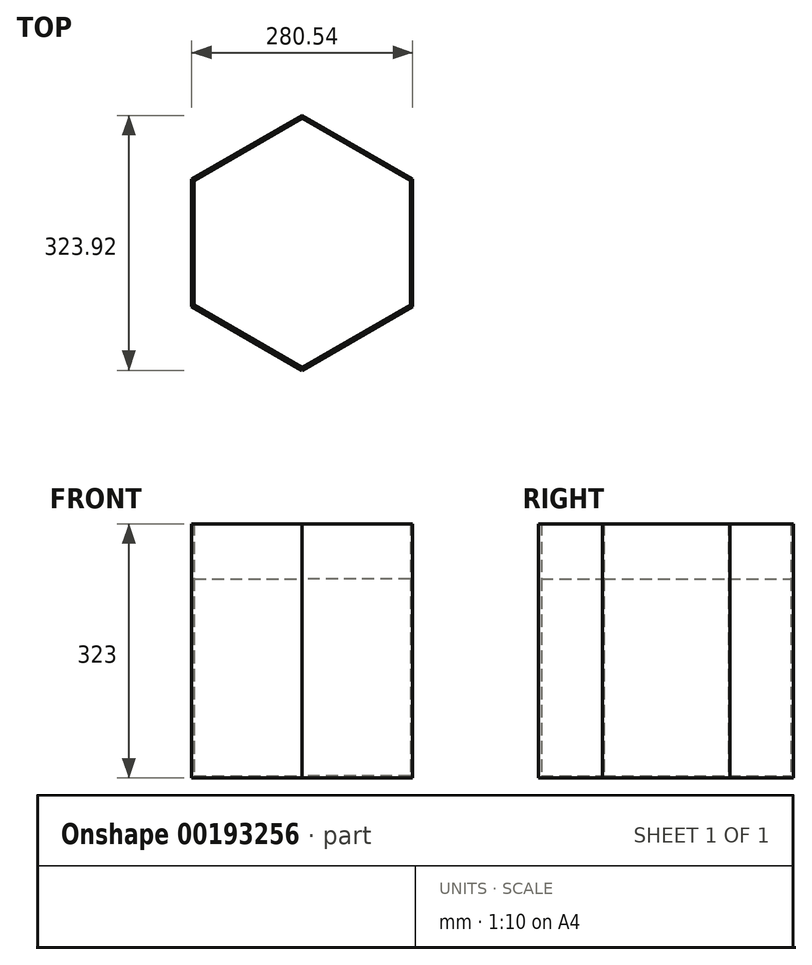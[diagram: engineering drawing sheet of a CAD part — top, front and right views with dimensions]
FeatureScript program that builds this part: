
annotation { "Feature Type Name" : "Feature", "Feature Type Description" : "" }
export const myFeature = defineFeature(function(context is Context, id is Id, definition is map)
    precondition{}
    {
        {
            var Q0;
            Q0=qCreatedBy(makeId("Top.planeOp"),FACE);
            var sketch = newSketch(context, id + "F0", { "sketchPlane" : qUnion([Q0])});
            skCircle(sketch, "E0.cCircle", {"center": v(0, 0) * mm, "radius": 158.5 * mm, "construction": true});
            skLineSegment(sketch, "E0.0", {"start": v(0, 158.5) * mm, "end": v(137.27, 79.25) * mm});
            skLineSegment(sketch, "E0.1", {"start": v(137.27, 79.25) * mm, "end": v(137.27, -79.25) * mm});
            skLineSegment(sketch, "E0.2", {"start": v(137.27, -79.25) * mm, "end": v(0, -158.5) * mm});
            skLineSegment(sketch, "E0.3", {"start": v(0, -158.5) * mm, "end": v(-137.27, -79.25) * mm});
            skLineSegment(sketch, "E0.4", {"start": v(-137.27, -79.25) * mm, "end": v(-137.27, 79.25) * mm});
            skLineSegment(sketch, "E0.5", {"start": v(-137.27, 79.25) * mm, "end": v(0, 158.5) * mm});
            skCircle(sketch, "E1.cCircle", {"center": v(0, 0) * mm, "radius": 161.96 * mm, "construction": true});
            skLineSegment(sketch, "E1.0", {"start": v(0, 161.96) * mm, "end": v(140.27, 80.98) * mm});
            skLineSegment(sketch, "E1.1", {"start": v(140.27, 80.98) * mm, "end": v(140.27, -80.98) * mm});
            skLineSegment(sketch, "E1.2", {"start": v(140.27, -80.98) * mm, "end": v(0, -161.96) * mm});
            skLineSegment(sketch, "E1.3", {"start": v(0, -161.96) * mm, "end": v(-140.27, -80.98) * mm});
            skLineSegment(sketch, "E1.4", {"start": v(-140.27, -80.98) * mm, "end": v(-140.27, 80.98) * mm});
            skLineSegment(sketch, "E1.5", {"start": v(-140.27, 80.98) * mm, "end": v(0, 161.96) * mm});
            skSolve(sketch);
        }
        {
            var Q0;
            Q0 = qSketchRegion(id + "F0", true);
            var Q1;
            Q1=makeQuery(id+"F0.imprint","IMPRINT",FACE,{"disambiguationData":[TD([[makeQuery(id+"F0.imprint","IMPRINT",EDGE,{"derivedFrom":sQuery(id+"F0.wireOp",EDGE,"E0.0")}),-1.0]])]});
            extrude(context, id + "F1", {"entities" : qUnion([Q0, Q1]), "depth" : 3 * mm});
        }
        {
            var Q0;
            Q0=makeQuery(id+"F1.opExtrude","CAP_FACE",FACE,{"disambiguationData":[OSD([sQuery(id+"F0.wireOp",EDGE,"E1.0"),sQuery(id+"F0.wireOp",EDGE,"E1.1"),sQuery(id+"F0.wireOp",EDGE,"E1.2"),sQuery(id+"F0.wireOp",EDGE,"E1.3"),sQuery(id+"F0.wireOp",EDGE,"E1.4"),sQuery(id+"F0.wireOp",EDGE,"E1.5")])],"isStart":false});
            var sketch = newSketch(context, id + "F2", { "sketchPlane" : qUnion([Q0])});
            skCircle(sketch, "E2.cCircle", {"center": v(0, 0) * mm, "radius": 161.96 * mm, "construction": true});
            skLineSegment(sketch, "E2.0", {"start": v(0, 161.96) * mm, "end": v(140.27, 80.98) * mm});
            skLineSegment(sketch, "E2.1", {"start": v(140.27, 80.98) * mm, "end": v(140.27, -80.98) * mm});
            skLineSegment(sketch, "E2.2", {"start": v(140.27, -80.98) * mm, "end": v(0, -161.96) * mm});
            skLineSegment(sketch, "E2.3", {"start": v(0, -161.96) * mm, "end": v(-140.27, -80.98) * mm});
            skLineSegment(sketch, "E2.4", {"start": v(-140.27, -80.98) * mm, "end": v(-140.27, 80.98) * mm});
            skLineSegment(sketch, "E2.5", {"start": v(-140.27, 80.98) * mm, "end": v(0, 161.96) * mm});
            skCircle(sketch, "E3.cCircle", {"center": v(0, 0) * mm, "radius": 158.5 * mm, "construction": true});
            skLineSegment(sketch, "E3.0", {"start": v(0, 158.5) * mm, "end": v(137.27, 79.25) * mm});
            skLineSegment(sketch, "E3.1", {"start": v(137.27, 79.25) * mm, "end": v(137.27, -79.25) * mm});
            skLineSegment(sketch, "E3.2", {"start": v(137.27, -79.25) * mm, "end": v(0, -158.5) * mm});
            skLineSegment(sketch, "E3.3", {"start": v(0, -158.5) * mm, "end": v(-137.27, -79.25) * mm});
            skLineSegment(sketch, "E3.4", {"start": v(-137.27, -79.25) * mm, "end": v(-137.27, 79.25) * mm});
            skLineSegment(sketch, "E3.5", {"start": v(-137.27, 79.25) * mm, "end": v(0, 158.5) * mm});
            skSolve(sketch);
        }
        {
            var Q0;
            Q0 = qSketchRegion(id + "F2", true);
            extrude(context, id + "F3", {"entities" : qUnion([Q0]), "operationType" : NewBodyOperationType.ADD, "depth" : 320 * mm});
        }
        {
            var Q0;
            Q0=makeQuery(id+"F1.opExtrude","CAP_FACE",FACE,{"disambiguationData":[OSD([sQuery(id+"F0.wireOp",EDGE,"E1.0"),sQuery(id+"F0.wireOp",EDGE,"E1.1"),sQuery(id+"F0.wireOp",EDGE,"E1.2"),sQuery(id+"F0.wireOp",EDGE,"E1.3"),sQuery(id+"F0.wireOp",EDGE,"E1.4"),sQuery(id+"F0.wireOp",EDGE,"E1.5")])],"isStart":false});
            var sketch = newSketch(context, id + "F4", { "sketchPlane" : qUnion([Q0])});
            skCircle(sketch, "E4.cCircle", {"center": v(0, 0) * mm, "radius": 158.5 * mm, "construction": true});
            skLineSegment(sketch, "E4.0", {"start": v(0, 158.5) * mm, "end": v(137.27, 79.25) * mm});
            skLineSegment(sketch, "E4.1", {"start": v(137.27, 79.25) * mm, "end": v(137.27, -79.25) * mm});
            skLineSegment(sketch, "E4.2", {"start": v(137.27, -79.25) * mm, "end": v(0, -158.5) * mm});
            skLineSegment(sketch, "E4.3", {"start": v(0, -158.5) * mm, "end": v(-137.27, -79.25) * mm});
            skLineSegment(sketch, "E4.4", {"start": v(-137.27, -79.25) * mm, "end": v(-137.27, 79.25) * mm});
            skLineSegment(sketch, "E4.5", {"start": v(-137.27, 79.25) * mm, "end": v(0, 158.5) * mm});
            skSolve(sketch);
        }
        {
            var Q0;
            Q0 = qSketchRegion(id + "F4", true);
            extrude(context, id + "F5", {"entities" : qUnion([Q0]), "depth" : 250 * mm});
        }
    });
